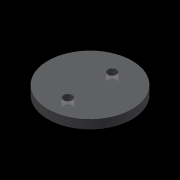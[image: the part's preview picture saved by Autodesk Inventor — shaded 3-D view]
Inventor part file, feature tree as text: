
AUTODESK INVENTOR PART (.ipt)
format: ipt  version: 2015 (Build 190159000, 159)  size: 82,944 bytes
history: native  units: mm
features: extrude x2, sketch x2
ambient origin geometry x8: Origin, YZ Plane, XZ Plane, XY Plane, X Axis, Y Axis, Z Axis, Center Point
bodies: Solid1 (feature_tree)
feature tree (4):
  extrude  "Extrusion1"  Depth=3.0mm TaperAngle=0.0deg
  extrude  "Extrusion4"  Depth=3.0mm
  sketch  "Sketch1"  dims[d0=28.5mm d3=3.0mm d4=0.0mm]
  sketch  "Sketch2"  dims[d22=9.5mm d31=3.0mm d33=3.0mm d34=15.0mm d35=7.5mm d36=10.0mm d37=0.0mm]
